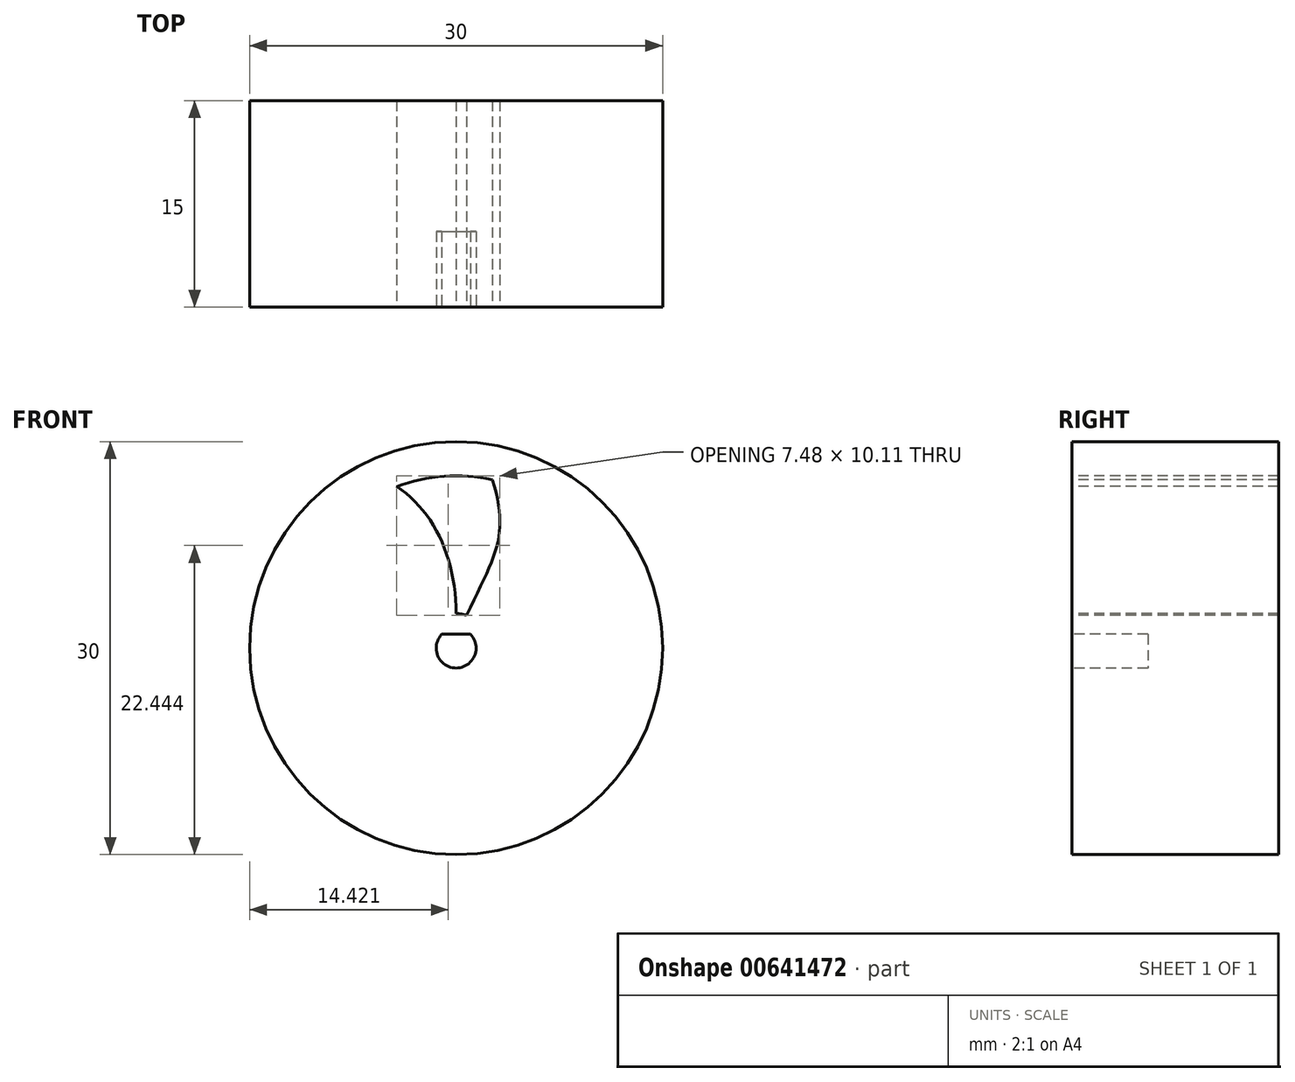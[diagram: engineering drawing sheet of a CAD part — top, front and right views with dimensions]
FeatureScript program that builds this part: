
annotation { "Feature Type Name" : "Feature", "Feature Type Description" : "" }
export const myFeature = defineFeature(function(context is Context, id is Id, definition is map)
    precondition{}
    {
        {
            var Q0;
            Q0=qCreatedBy(makeId("Front.planeOp"),FACE);
            var sketch = newSketch(context, id + "F0", { "sketchPlane" : qUnion([Q0])});
            skCircle(sketch, "E0", {"center": v(0, 0) * mm, "radius": 15 * mm});
            skSolve(sketch);
        }
        {
            var Q0;
            Q0=makeQuery(id+"F0.imprint","IMPRINT",FACE,{"disambiguationData":[TD([[makeQuery(id+"F0.imprint","IMPRINT",EDGE,{"derivedFrom":sQuery(id+"F0.wireOp",EDGE,"E0")}),1.0]])]});
            extrude(context, id + "F1", {"entities" : qUnion([Q0]), "oppositeDirection" : true, "depth" : 15 * mm, "offsetDistance" : 25 * mm});
        }
        {
            var Q0;
            Q0=makeQuery(id+"F1.opExtrude","CAP_FACE",FACE,{"disambiguationData":[OSD([sQuery(id+"F0.wireOp",EDGE,"E0")])],"isStart":true});
            var sketch = newSketch(context, id + "F2", { "sketchPlane" : qUnion([Q0])});
            skCircle(sketch, "E1", {"center": v(0, 0) * mm, "radius": 1.45 * mm});
            skLineSegment(sketch, "E2", {"start": v(-1.05, 1) * mm, "end": v(1.05, 1) * mm});
            skSolve(sketch);
        }
        {
            var Q0;
            {var subQ0=sQuery(id+"F2.wireOp",EDGE,"E2");Q0=makeQuery(id+"F2.imprint","IMPRINT",FACE,{"disambiguationData":[TD([[makeQuery(id+"F2.imprint","IMPRINT",EDGE,{"derivedFrom":subQ0}),-1.0]])]});}
            extrude(context, id + "F3", {"entities" : qUnion([Q0]), "operationType" : NewBodyOperationType.REMOVE, "oppositeDirection" : true, "depth" : 5.5 * mm, "offsetDistance" : 25 * mm});
        }
        {
            var Q0;
            Q0=makeQuery(id+"F1.opExtrude","CAP_FACE",FACE,{"disambiguationData":[OSD([sQuery(id+"F0.wireOp",EDGE,"E0")])],"isStart":true});
            var sketch = newSketch(context, id + "F4", { "sketchPlane" : qUnion([Q0])});
            skFitSpline(sketch, "E3", {"points": [v(-4.32, 11.73) * mm, v(0, 2.5) * mm], "startDerivative": vector(8.25, -5.38) * mm, "endDerivative": vector(0, -11.75) * mm});
            skFitSpline(sketch, "E4", {"points": [v(2.63, 12.22) * mm, v(0.74, 2.39) * mm], "startDerivative": vector(3.6, -11.66) * mm, "endDerivative": vector(-6.77, -13.56) * mm});
            skCircle(sketch, "E5", {"center": v(0, 0) * mm, "radius": 2.5 * mm});
            skCircle(sketch, "E6", {"center": v(0, 0) * mm, "radius": 12.5 * mm});
            skSolve(sketch);
        }
        {
            var Q0;
            {var subQ0=sQuery(id+"F4.wireOp",EDGE,"E3");Q0=makeQuery(id+"F4.imprint","IMPRINT",FACE,{"disambiguationData":[TD([[makeQuery(id+"F4.imprint","IMPRINT",EDGE,{"derivedFrom":subQ0}),1.0]])]});}
            extrude(context, id + "F5", {"entities" : qUnion([Q0]), "operationType" : NewBodyOperationType.REMOVE, "endBound" : BoundingType.THROUGH_ALL, "oppositeDirection" : true, "depth" : 25 * mm, "offsetDistance" : 25 * mm});
        }
    });
